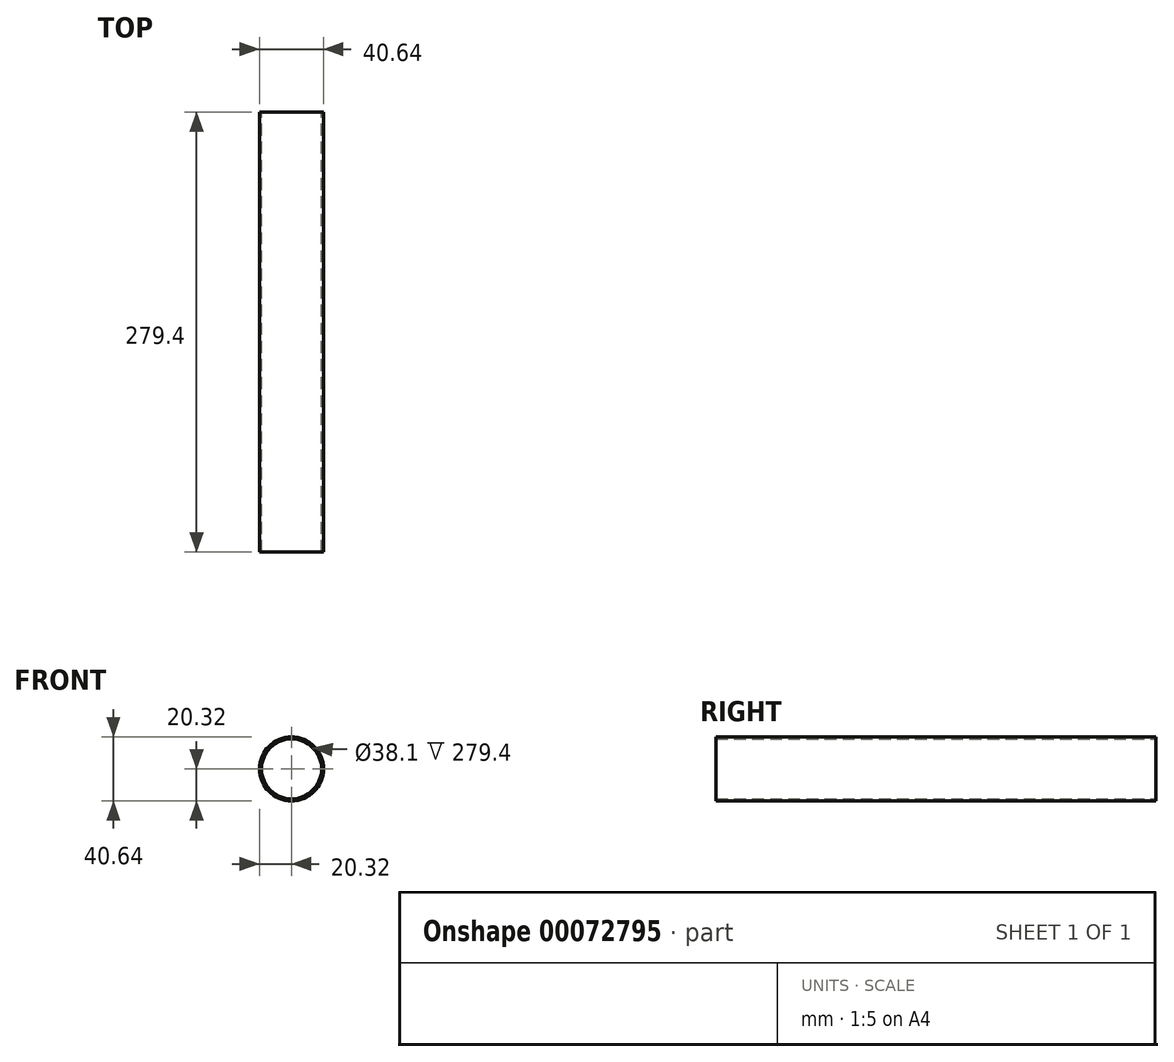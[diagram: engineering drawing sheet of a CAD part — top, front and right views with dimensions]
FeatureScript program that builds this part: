
annotation { "Feature Type Name" : "Feature", "Feature Type Description" : "" }
export const myFeature = defineFeature(function(context is Context, id is Id, definition is map)
    precondition{}
    {
        {
            var Q0;
            Q0=qCreatedBy(makeId("Front.planeOp"),FACE);
            var sketch = newSketch(context, id + "F0", { "sketchPlane" : qUnion([Q0])});
            skCircle(sketch, "E0", {"center": v(0, 0) * mm, "radius": 19.05 * mm});
            skCircle(sketch, "E1", {"center": v(0, 0) * mm, "radius": 20.32 * mm});
            skSolve(sketch);
        }
        {
            var Q0;
            Q0=makeQuery(id+"F0.imprint","IMPRINT",FACE,{"disambiguationData":[TD([[makeQuery(id+"F0.imprint","IMPRINT",EDGE,{"derivedFrom":sQuery(id+"F0.wireOp",EDGE,"E0")}),-1.0]])]});
            extrude(context, id + "F1", {"entities" : qUnion([Q0]), "depth" : 279.4 * mm});
        }
    });
